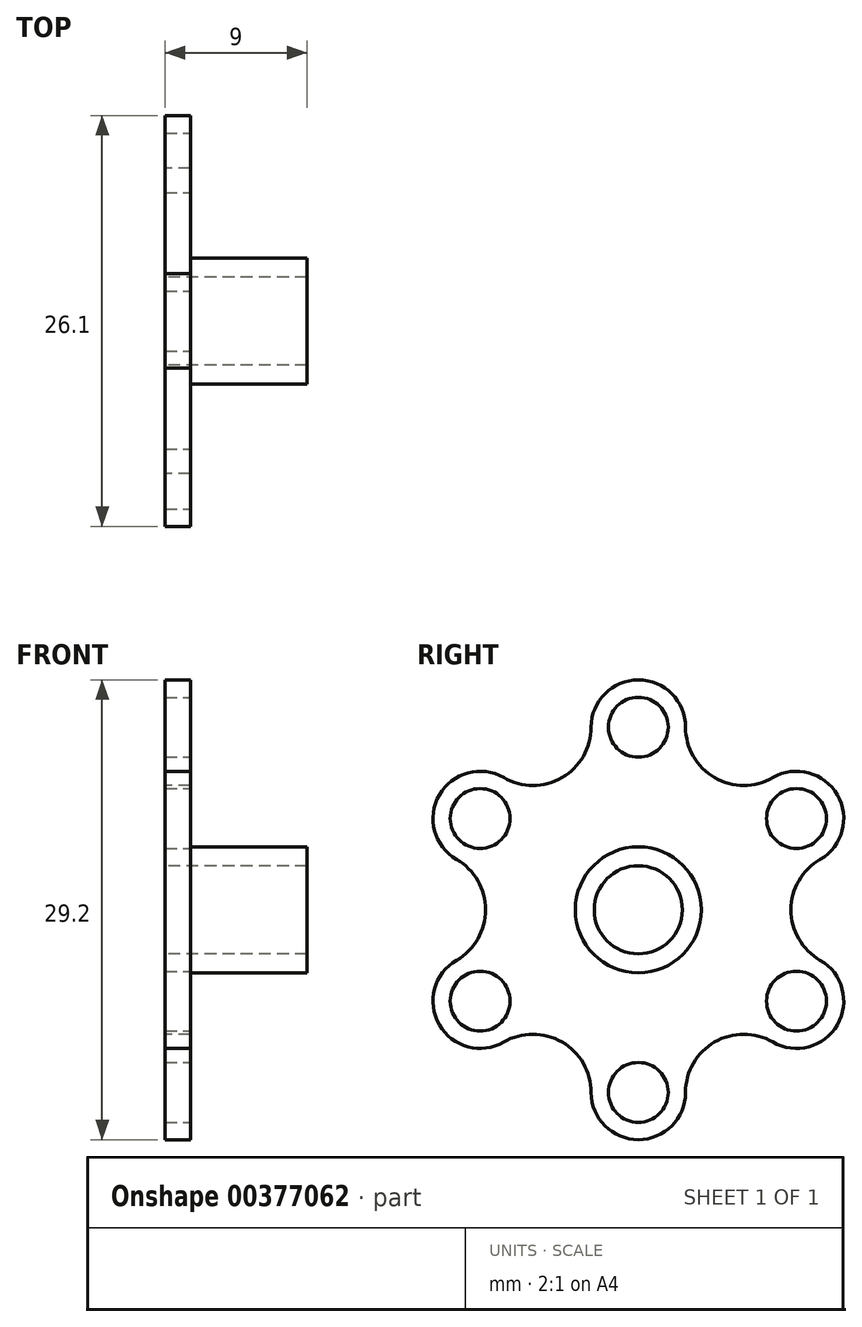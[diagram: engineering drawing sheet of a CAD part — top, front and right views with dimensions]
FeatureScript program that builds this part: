
annotation { "Feature Type Name" : "Feature", "Feature Type Description" : "" }
export const myFeature = defineFeature(function(context is Context, id is Id, definition is map)
    precondition{}
    {
        {
            var Q0;
            Q0=qCreatedBy(makeId("Front.planeOp"),FACE);
            var sketch = newSketch(context, id + "F0", { "sketchPlane" : qUnion([Q0])});
            skLineSegment(sketch, "E0", {"start": v(-1.6, 2.8) * mm, "end": v(-1.6, 14.6) * mm});
            skLineSegment(sketch, "E1", {"start": v(-1.6, 14.6) * mm, "end": v(0, 14.6) * mm});
            skLineSegment(sketch, "E2", {"start": v(-1.6, 2.8) * mm, "end": v(7.4, 2.8) * mm});
            skLineSegment(sketch, "E3", {"start": v(-1.6, 11.6) * mm, "end": v(0, 11.6) * mm, "construction": true});
            skLineSegment(sketch, "E4", {"start": v(7.4, 2.8) * mm, "end": v(7.4, 4) * mm});
            skLineSegment(sketch, "E5", {"start": v(7.4, 4) * mm, "end": v(0, 4) * mm});
            skLineSegment(sketch, "E6", {"start": v(0, 4) * mm, "end": v(0, 14.6) * mm});
            skLineSegment(sketch, "E7", {"start": v(0, 0) * mm, "end": v(7.4, 0) * mm, "construction": true});
            skSolve(sketch);
        }
        {
            var Q0;
            Q0 = qSketchRegion(id + "F0", true);
            var Q1;
            Q1=sQuery(id+"F0.wireOp",EDGE,"E7");
            revolve(context, id + "F1", {"entities" : qUnion([Q0]), "axis" : qUnion([Q1]), "revolveType" : RevolveType.FULL});
        }
        {
            var Q0;
            Q0=qCreatedBy(makeId("Right.planeOp"),FACE);
            var sketch = newSketch(context, id + "F2", { "sketchPlane" : qUnion([Q0])});
            skCircle(sketch, "E8", {"center": v(0, 11.6) * mm, "radius": 1.9 * mm});
            skCircle(sketch, "E9.1.0", {"center": v(-10.05, 5.8) * mm, "radius": 1.9 * mm});
            skCircle(sketch, "E9.2.0", {"center": v(-10.05, -5.8) * mm, "radius": 1.9 * mm});
            skCircle(sketch, "E9.3.0", {"center": v(0, -11.6) * mm, "radius": 1.9 * mm});
            skCircle(sketch, "E9.4.0", {"center": v(10.05, -5.8) * mm, "radius": 1.9 * mm});
            skCircle(sketch, "E9.5.0", {"center": v(10.05, 5.8) * mm, "radius": 1.9 * mm});
            skPoint(sketch, "E9.center", {"position": v(0, 0) * mm});
            skSolve(sketch);
        }
        {
            var Q0;
            Q0 = qSketchRegion(id + "F2", true);
            extrude(context, id + "F3", {"entities" : qUnion([Q0]), "operationType" : NewBodyOperationType.REMOVE, "endBound" : BoundingType.UP_TO_NEXT, "oppositeDirection" : true, "depth" : 25 * mm});
        }
        {
            var Q0;
            Q0=qCreatedBy(makeId("Right.planeOp"),FACE);
            var sketch = newSketch(context, id + "F4", { "sketchPlane" : qUnion([Q0])});
            skArc(sketch, "E10", {"start": v(3, 11.6) * mm, "mid": v(0, 14.6) * mm, "end": v(-3, 11.6) * mm});
            skLineSegment(sketch, "E11", {"start": v(0, 0) * mm, "end": v(10.05, 5.8) * mm, "construction": true});
            skLineSegment(sketch, "E12", {"start": v(8.55, 8.4) * mm, "end": v(11.55, 3.2) * mm, "construction": true});
            skLineSegment(sketch, "E13", {"start": v(-3, 11.6) * mm, "end": v(3, 11.6) * mm, "construction": true});
            skPoint(sketch, "E14", {"position": v(10.05, 5.8) * mm});
            skArc(sketch, "E15", {"start": v(3, 11.6) * mm, "mid": v(4.85, 8.4) * mm, "end": v(8.55, 8.4) * mm});
            skArc(sketch, "E16.1.0", {"start": v(-8.55, 8.4) * mm, "mid": v(-12.64, 7.3) * mm, "end": v(-11.55, 3.2) * mm});
            skArc(sketch, "E16.1.1", {"start": v(-8.55, 8.4) * mm, "mid": v(-4.85, 8.4) * mm, "end": v(-3, 11.6) * mm});
            skArc(sketch, "E16.2.0", {"start": v(-11.55, -3.2) * mm, "mid": v(-12.64, -7.3) * mm, "end": v(-8.55, -8.4) * mm});
            skArc(sketch, "E16.2.1", {"start": v(-11.55, -3.2) * mm, "mid": v(-9.7, 0) * mm, "end": v(-11.55, 3.2) * mm});
            skArc(sketch, "E16.3.0", {"start": v(-3, -11.6) * mm, "mid": v(0, -14.6) * mm, "end": v(3, -11.6) * mm});
            skArc(sketch, "E16.3.1", {"start": v(-3, -11.6) * mm, "mid": v(-4.85, -8.4) * mm, "end": v(-8.55, -8.4) * mm});
            skArc(sketch, "E16.4.0", {"start": v(8.55, -8.4) * mm, "mid": v(12.64, -7.3) * mm, "end": v(11.55, -3.2) * mm});
            skArc(sketch, "E16.4.1", {"start": v(8.55, -8.4) * mm, "mid": v(4.85, -8.4) * mm, "end": v(3, -11.6) * mm});
            skArc(sketch, "E16.5.0", {"start": v(11.55, 3.2) * mm, "mid": v(12.64, 7.3) * mm, "end": v(8.55, 8.4) * mm});
            skArc(sketch, "E16.5.1", {"start": v(11.55, 3.2) * mm, "mid": v(9.7, 0) * mm, "end": v(11.55, -3.2) * mm});
            skPoint(sketch, "E16.center", {"position": v(0, 0) * mm});
            skSolve(sketch);
        }
        {
            var Q0;
            Q0 = qSketchRegion(id + "F4", true);
            extrude(context, id + "F5", {"entities" : qUnion([Q0]), "operationType" : NewBodyOperationType.INTERSECT, "endBound" : BoundingType.THROUGH_ALL, "depth" : 25 * mm, "hasSecondDirection" : true, "secondDirectionBound" : SecondDirectionBoundingType.THROUGH_ALL, "secondDirectionOppositeDirection" : true, "secondDirectionDepth" : 25 * mm});
        }
    });
